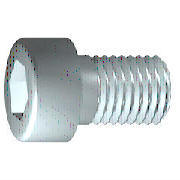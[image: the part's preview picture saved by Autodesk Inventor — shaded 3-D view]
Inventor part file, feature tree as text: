
AUTODESK INVENTOR PART (.ipt)
format: ipt  version: 2024.3 (Build 283343000, 343)  size: 194,560 bytes
history: native  units: mm (DEFAULTED — no unit token found)
features: extrude x1, plane x1, fillet x1
ambient origin geometry x7: Origin, YZ Plane, XY Plane, X Axis, Y Axis, Z Axis, Center Point
bodies: Solid1 (feature_tree), Body (feature_tree)
feature tree (3):
  extrude  "Slot"  Depth=9.5mm
  plane  "Work Plane1"
  fillet  "Fillet2"  Radius=0.61355mm
